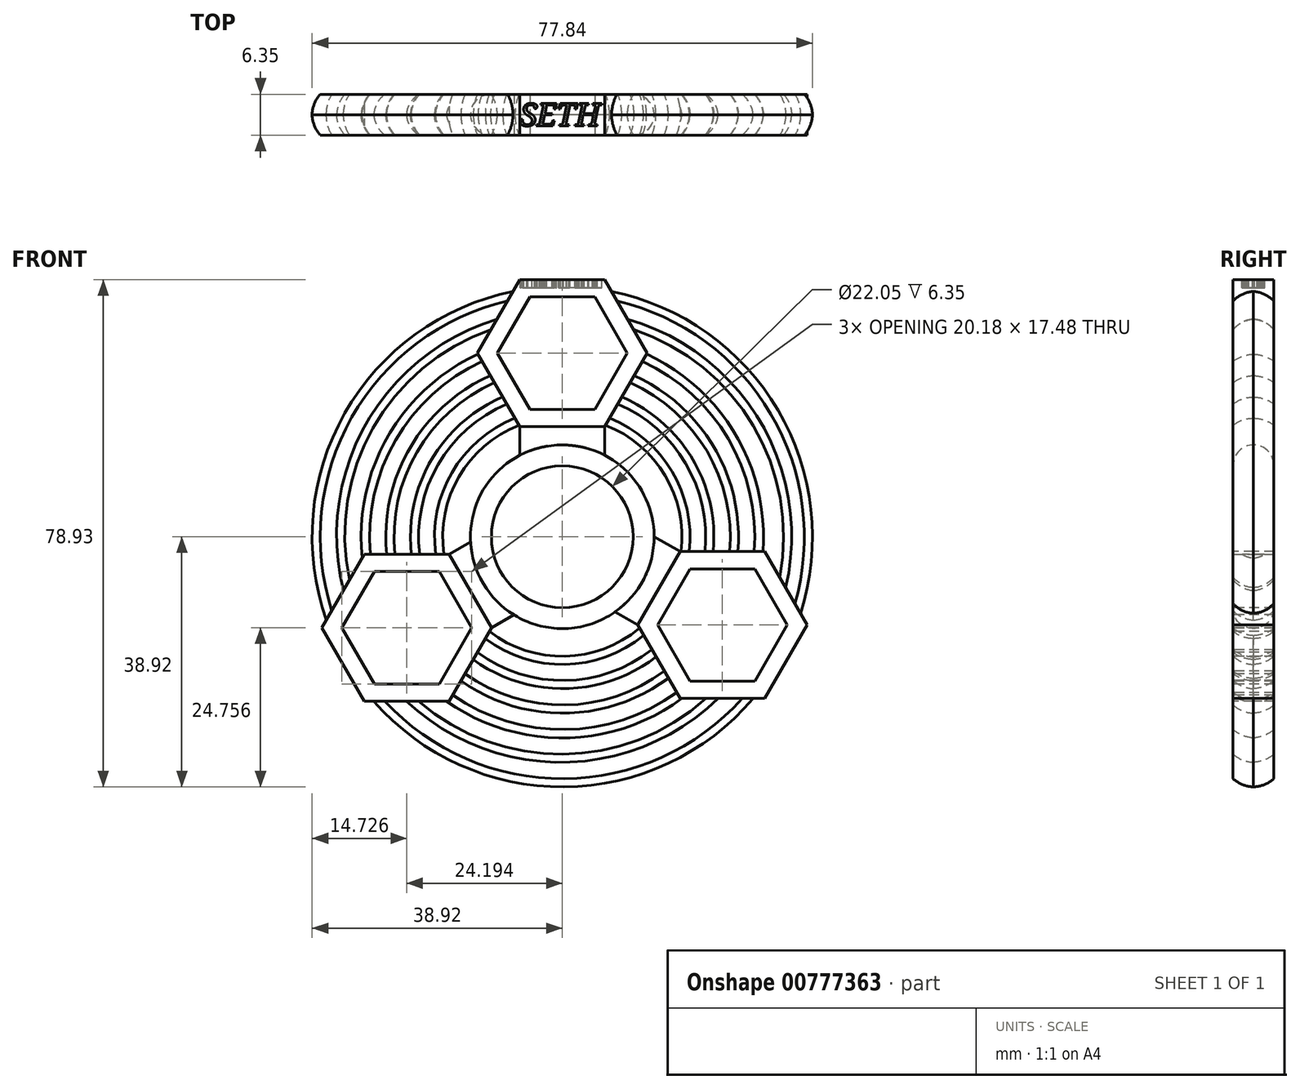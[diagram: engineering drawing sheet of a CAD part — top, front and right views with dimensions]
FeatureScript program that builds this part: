
annotation { "Feature Type Name" : "Feature", "Feature Type Description" : "" }
export const myFeature = defineFeature(function(context is Context, id is Id, definition is map)
    precondition{}
    {
        {
            var Q0;
            Q0=qCreatedBy(makeId("Front.planeOp"),FACE);
            var sketch = newSketch(context, id + "F0", { "sketchPlane" : qUnion([Q0])});
            skCircle(sketch, "E0", {"center": v(0, 0) * mm, "radius": 11.02 * mm});
            skCircle(sketch, "E1", {"center": v(0, 0) * mm, "radius": 14.29 * mm});
            skCircle(sketch, "E2.cCircle", {"center": v(0, 28.58) * mm, "radius": 8.74 * mm, "construction": true});
            skLineSegment(sketch, "E2.0", {"start": v(5.04, 19.84) * mm, "end": v(-5.04, 19.84) * mm});
            skLineSegment(sketch, "E2.1", {"start": v(-5.04, 19.84) * mm, "end": v(-10.09, 28.57) * mm});
            skLineSegment(sketch, "E2.2", {"start": v(-10.09, 28.58) * mm, "end": v(-5.04, 37.31) * mm});
            skLineSegment(sketch, "E2.3", {"start": v(-5.04, 37.31) * mm, "end": v(5.04, 37.31) * mm});
            skLineSegment(sketch, "E2.4", {"start": v(5.04, 37.31) * mm, "end": v(10.09, 28.58) * mm});
            skLineSegment(sketch, "E2.5", {"start": v(10.09, 28.57) * mm, "end": v(5.04, 19.84) * mm});
            skPoint(sketch, "E2.0.midPoint", {"position": v(0, 19.84) * mm});
            skCircle(sketch, "E3.cCircle", {"center": v(0, 28.58) * mm, "radius": 11.43 * mm, "construction": true});
            skLineSegment(sketch, "E3.0", {"start": v(6.6, 17.15) * mm, "end": v(-6.6, 17.14) * mm});
            skLineSegment(sketch, "E3.1", {"start": v(-6.6, 17.15) * mm, "end": v(-13.2, 28.57) * mm});
            skLineSegment(sketch, "E3.2", {"start": v(-13.2, 28.58) * mm, "end": v(-6.6, 40) * mm});
            skLineSegment(sketch, "E3.3", {"start": v(-6.6, 40) * mm, "end": v(6.6, 40) * mm});
            skLineSegment(sketch, "E3.4", {"start": v(6.6, 40) * mm, "end": v(13.2, 28.58) * mm});
            skLineSegment(sketch, "E3.5", {"start": v(13.2, 28.57) * mm, "end": v(6.6, 17.15) * mm});
            skPoint(sketch, "E3.0.midPoint", {"position": v(0, 17.15) * mm});
            skCircle(sketch, "E4.1.0", {"center": v(-24.2, -14.16) * mm, "radius": 8.74 * mm, "construction": true});
            skLineSegment(sketch, "E4.1.1", {"start": v(-19.15, -5.43) * mm, "end": v(-14.1, -14.16) * mm});
            skPoint(sketch, "E4.1.2", {"position": v(-14.3, -8.45) * mm});
            skLineSegment(sketch, "E4.1.3", {"start": v(-19.15, -22.9) * mm, "end": v(-29.24, -22.9) * mm});
            skLineSegment(sketch, "E4.1.4", {"start": v(-30.8, -2.73) * mm, "end": v(-17.6, -2.73) * mm});
            skLineSegment(sketch, "E4.1.5", {"start": v(-37.4, -14.16) * mm, "end": v(-30.8, -2.73) * mm});
            skLineSegment(sketch, "E4.1.6", {"start": v(-30.8, -25.6) * mm, "end": v(-37.4, -14.16) * mm});
            skLineSegment(sketch, "E4.1.7", {"start": v(-14.1, -14.16) * mm, "end": v(-19.15, -22.9) * mm});
            skLineSegment(sketch, "E4.1.8", {"start": v(-29.24, -22.9) * mm, "end": v(-34.28, -14.16) * mm});
            skLineSegment(sketch, "E4.1.9", {"start": v(-34.28, -14.16) * mm, "end": v(-29.24, -5.43) * mm});
            skLineSegment(sketch, "E4.1.10", {"start": v(-29.24, -5.43) * mm, "end": v(-19.15, -5.43) * mm});
            skCircle(sketch, "E4.1.11", {"center": v(-24.2, -14.16) * mm, "radius": 11.43 * mm, "construction": true});
            skLineSegment(sketch, "E4.1.12", {"start": v(-17.6, -2.73) * mm, "end": v(-11, -14.16) * mm});
            skLineSegment(sketch, "E4.1.13", {"start": v(-11, -14.16) * mm, "end": v(-17.6, -25.6) * mm});
            skLineSegment(sketch, "E4.1.14", {"start": v(-17.6, -25.6) * mm, "end": v(-30.8, -25.6) * mm});
            skPoint(sketch, "E4.1.15", {"position": v(-16.63, -9.8) * mm});
            skCircle(sketch, "E4.2.0", {"center": v(24.92, -13.75) * mm, "radius": 8.74 * mm, "construction": true});
            skLineSegment(sketch, "E4.2.1", {"start": v(14.83, -13.75) * mm, "end": v(19.87, -5) * mm});
            skPoint(sketch, "E4.2.2", {"position": v(15.02, -8.03) * mm});
            skLineSegment(sketch, "E4.2.3", {"start": v(29.96, -5) * mm, "end": v(35, -13.75) * mm});
            skLineSegment(sketch, "E4.2.4", {"start": v(18.32, -25.18) * mm, "end": v(11.72, -13.75) * mm});
            skLineSegment(sketch, "E4.2.5", {"start": v(31.51, -25.18) * mm, "end": v(18.32, -25.18) * mm});
            skLineSegment(sketch, "E4.2.6", {"start": v(38.11, -13.75) * mm, "end": v(31.51, -25.18) * mm});
            skLineSegment(sketch, "E4.2.7", {"start": v(19.87, -5) * mm, "end": v(29.96, -5) * mm});
            skLineSegment(sketch, "E4.2.8", {"start": v(35, -13.75) * mm, "end": v(29.96, -22.48) * mm});
            skLineSegment(sketch, "E4.2.9", {"start": v(29.96, -22.48) * mm, "end": v(19.87, -22.48) * mm});
            skLineSegment(sketch, "E4.2.10", {"start": v(19.87, -22.48) * mm, "end": v(14.83, -13.75) * mm});
            skCircle(sketch, "E4.2.11", {"center": v(24.92, -13.75) * mm, "radius": 11.43 * mm, "construction": true});
            skLineSegment(sketch, "E4.2.12", {"start": v(11.72, -13.75) * mm, "end": v(18.32, -2.32) * mm});
            skLineSegment(sketch, "E4.2.13", {"start": v(18.32, -2.32) * mm, "end": v(31.51, -2.32) * mm});
            skLineSegment(sketch, "E4.2.14", {"start": v(31.51, -2.32) * mm, "end": v(38.11, -13.75) * mm});
            skPoint(sketch, "E4.2.15", {"position": v(17.35, -9.38) * mm});
            skPoint(sketch, "E4.center", {"position": v(0.24, 0.22) * mm});
            skSolve(sketch);
        }
        {
            var Q0;
            Q0=qCreatedBy(makeId("Front.planeOp"),FACE);
            var sketch = newSketch(context, id + "F1", { "sketchPlane" : qUnion([Q0])});
            skLineSegment(sketch, "E5.0", {"start": v(-5.04, 19.84) * mm, "end": v(-10.09, 28.57) * mm});
            skLineSegment(sketch, "E5.1", {"start": v(5.04, 19.84) * mm, "end": v(-5.04, 19.84) * mm});
            skLineSegment(sketch, "E5.2", {"start": v(-10.09, 28.58) * mm, "end": v(-5.04, 37.31) * mm});
            skCircle(sketch, "E5.3", {"center": v(0, 28.58) * mm, "radius": 8.74 * mm});
            skLineSegment(sketch, "E5.4", {"start": v(-5.04, 37.31) * mm, "end": v(5.04, 37.31) * mm});
            skLineSegment(sketch, "E5.5", {"start": v(5.04, 37.31) * mm, "end": v(10.09, 28.58) * mm});
            skLineSegment(sketch, "E5.6", {"start": v(18.32, -2.32) * mm, "end": v(31.51, -2.32) * mm});
            skCircle(sketch, "E5.7", {"center": v(-24.2, -14.16) * mm, "radius": 11.43 * mm});
            skCircle(sketch, "E5.8", {"center": v(0, 0) * mm, "radius": 14.29 * mm});
            skCircle(sketch, "E5.9", {"center": v(0, 0) * mm, "radius": 11.02 * mm});
            skLineSegment(sketch, "E5.10", {"start": v(13.2, 28.57) * mm, "end": v(6.6, 17.15) * mm});
            skLineSegment(sketch, "E5.11", {"start": v(6.6, 40) * mm, "end": v(13.2, 28.58) * mm});
            skLineSegment(sketch, "E5.12", {"start": v(-6.6, 40) * mm, "end": v(6.6, 40) * mm});
            skLineSegment(sketch, "E5.13", {"start": v(38.11, -13.75) * mm, "end": v(31.51, -25.18) * mm});
            skLineSegment(sketch, "E5.14", {"start": v(-30.8, -2.73) * mm, "end": v(-17.6, -2.73) * mm});
            skLineSegment(sketch, "E5.15", {"start": v(10.09, 28.57) * mm, "end": v(8.57, 25.94) * mm});
            skCircle(sketch, "E5.16", {"center": v(0, 28.58) * mm, "radius": 11.43 * mm});
            skLineSegment(sketch, "E5.17", {"start": v(6.6, 17.15) * mm, "end": v(-6.6, 17.14) * mm});
            skLineSegment(sketch, "E5.18", {"start": v(-6.6, 17.15) * mm, "end": v(-13.2, 28.57) * mm});
            skLineSegment(sketch, "E5.19", {"start": v(-13.2, 28.58) * mm, "end": v(-6.6, 40) * mm});
            skLineSegment(sketch, "E5.20", {"start": v(31.51, -2.32) * mm, "end": v(38.11, -13.75) * mm});
            skLineSegment(sketch, "E5.21", {"start": v(-17.6, -2.73) * mm, "end": v(-11, -14.16) * mm});
            skLineSegment(sketch, "E5.22", {"start": v(19.87, -22.48) * mm, "end": v(14.83, -13.75) * mm});
            skLineSegment(sketch, "E5.23", {"start": v(-29.24, -22.9) * mm, "end": v(-34.28, -14.16) * mm});
            skLineSegment(sketch, "E5.24", {"start": v(-37.4, -14.16) * mm, "end": v(-30.8, -2.73) * mm});
            skLineSegment(sketch, "E5.25", {"start": v(19.87, -5) * mm, "end": v(29.96, -5) * mm});
            skLineSegment(sketch, "E5.26", {"start": v(-17.6, -25.6) * mm, "end": v(-30.8, -25.6) * mm});
            skCircle(sketch, "E5.27", {"center": v(-24.2, -14.16) * mm, "radius": 8.74 * mm});
            skLineSegment(sketch, "E5.28", {"start": v(29.96, -5) * mm, "end": v(35, -13.75) * mm});
            skLineSegment(sketch, "E5.29", {"start": v(-11, -14.16) * mm, "end": v(-17.6, -25.6) * mm});
            skCircle(sketch, "E5.30", {"center": v(24.92, -13.75) * mm, "radius": 11.43 * mm});
            skLineSegment(sketch, "E5.31", {"start": v(-34.28, -14.16) * mm, "end": v(-29.24, -5.43) * mm});
            skLineSegment(sketch, "E5.32", {"start": v(-30.8, -25.6) * mm, "end": v(-37.4, -14.16) * mm});
            skCircle(sketch, "E5.33", {"center": v(24.92, -13.75) * mm, "radius": 8.74 * mm});
            skLineSegment(sketch, "E5.34", {"start": v(35, -13.75) * mm, "end": v(29.96, -22.48) * mm});
            skLineSegment(sketch, "E5.35", {"start": v(-19.15, -5.43) * mm, "end": v(-14.1, -14.16) * mm});
            skLineSegment(sketch, "E5.36", {"start": v(18.32, -25.18) * mm, "end": v(11.72, -13.75) * mm});
            skLineSegment(sketch, "E5.37", {"start": v(11.72, -13.75) * mm, "end": v(18.32, -2.32) * mm});
            skLineSegment(sketch, "E5.38", {"start": v(-29.24, -5.43) * mm, "end": v(-19.15, -5.43) * mm});
            skLineSegment(sketch, "E5.39", {"start": v(-14.1, -14.16) * mm, "end": v(-19.15, -22.9) * mm});
            skLineSegment(sketch, "E5.40", {"start": v(14.83, -13.75) * mm, "end": v(19.87, -5) * mm});
            skLineSegment(sketch, "E5.41", {"start": v(29.96, -22.48) * mm, "end": v(19.87, -22.48) * mm});
            skLineSegment(sketch, "E5.42", {"start": v(-19.15, -22.9) * mm, "end": v(-29.24, -22.9) * mm});
            skLineSegment(sketch, "E5.43", {"start": v(31.51, -25.18) * mm, "end": v(18.32, -25.18) * mm});
            skArc(sketch, "E6.trimOffspring", {"start": v(-13.85, -19.1) * mm, "mid": v(0.43, -23.64) * mm, "end": v(14.57, -18.7) * mm});
            skArc(sketch, "E7.trimOffspring", {"start": v(-13.2, -18) * mm, "mid": v(0.43, -22.36) * mm, "end": v(13.93, -17.58) * mm});
            skArc(sketch, "E8.trimOffspring", {"start": v(-15.13, -21.32) * mm, "mid": v(0.43, -26.18) * mm, "end": v(15.85, -20.9) * mm});
            skArc(sketch, "E9.trimOffspring", {"start": v(-15.77, -22.43) * mm, "mid": v(0.43, -27.45) * mm, "end": v(16.5, -22.02) * mm});
            skArc(sketch, "E10.trimOffspring", {"start": v(22.19, -2.32) * mm, "mid": v(19.2, 11.4) * mm, "end": v(8.62, 20.65) * mm});
            skArc(sketch, "E11.trimOffspring", {"start": v(23.47, -2.32) * mm, "mid": v(20.3, 12.04) * mm, "end": v(9.26, 21.76) * mm});
            skArc(sketch, "E12.trimOffspring", {"start": v(26.03, -2.32) * mm, "mid": v(22.5, 13.31) * mm, "end": v(10.54, 23.97) * mm});
            skArc(sketch, "E13.trimOffspring", {"start": v(27.31, -2.32) * mm, "mid": v(23.6, 13.95) * mm, "end": v(11.18, 25.08) * mm});
            skArc(sketch, "E14.trimOffspring", {"start": v(-11.18, 25.08) * mm, "mid": v(-23.74, 13.78) * mm, "end": v(-27.31, -2.73) * mm});
            skArc(sketch, "E15.trimOffspring", {"start": v(-10.54, 23.97) * mm, "mid": v(-22.63, 13.14) * mm, "end": v(-26.03, -2.73) * mm});
            skArc(sketch, "E16.trimOffspring", {"start": v(-9.26, 21.76) * mm, "mid": v(-20.43, 11.87) * mm, "end": v(-23.47, -2.73) * mm});
            skArc(sketch, "E17.trimOffspring", {"start": v(-8.62, 20.65) * mm, "mid": v(-19.33, 11.23) * mm, "end": v(-22.19, -2.73) * mm});
            skArc(sketch, "E18.trimOffspring", {"start": v(-22.37, -25.6) * mm, "mid": v(0.08, -33.83) * mm, "end": v(22.37, -25.18) * mm});
            skArc(sketch, "E19.trimOffspring", {"start": v(-24.25, -25.6) * mm, "mid": v(0.08, -35.1) * mm, "end": v(24.25, -25.18) * mm});
            skArc(sketch, "E20.trimOffspring", {"start": v(-17.05, -24.65) * mm, "mid": v(0.43, -30) * mm, "end": v(17.77, -24.23) * mm});
            skArc(sketch, "E21.trimOffspring", {"start": v(34.76, -7.93) * mm, "mid": v(30.82, 17.9) * mm, "end": v(10.15, 33.86) * mm});
            skArc(sketch, "E22.trimOffspring", {"start": v(33.82, -6.3) * mm, "mid": v(29.73, 17.25) * mm, "end": v(11.09, 32.23) * mm});
            skArc(sketch, "E23.trimOffspring", {"start": v(29.87, -2.32) * mm, "mid": v(25.81, 15.22) * mm, "end": v(12.46, 27.3) * mm});
            skArc(sketch, "E24.trimOffspring", {"start": v(-10.15, 33.86) * mm, "mid": v(-30.55, 17.54) * mm, "end": v(-34.03, -8.35) * mm});
            skArc(sketch, "E25.trimOffspring", {"start": v(-11.09, 32.23) * mm, "mid": v(-29.45, 16.9) * mm, "end": v(-33.1, -6.72) * mm});
            skArc(sketch, "E26.trimOffspring", {"start": v(-12.46, 27.3) * mm, "mid": v(-25.94, 15.05) * mm, "end": v(-29.87, -2.73) * mm});
            skLineSegment(sketch, "E27", {"start": v(-6.6, 17.14) * mm, "end": v(-6.6, 12.67) * mm});
            skLineSegment(sketch, "E28", {"start": v(6.6, 17.15) * mm, "end": v(6.6, 12.67) * mm});
            skLineSegment(sketch, "E29", {"start": v(11.72, -13.75) * mm, "end": v(8.19, -11.7) * mm});
            skLineSegment(sketch, "E30", {"start": v(18.32, -2.32) * mm, "end": v(14.29, 0) * mm});
            skLineSegment(sketch, "E31", {"start": v(-17.6, -2.73) * mm, "end": v(-12.84, 0) * mm});
            skLineSegment(sketch, "E32", {"start": v(-11, -14.16) * mm, "end": v(-7.51, -12.15) * mm});
            skLineSegment(sketch, "E33.trimOffspring", {"start": v(7.92, 24.81) * mm, "end": v(5.04, 19.84) * mm});
            skLineSegment(sketch, "E34", {"start": v(7.92, 24.81) * mm, "end": v(8.57, 25.94) * mm});
            skArc(sketch, "E35", {"start": v(-11.98, -15.86) * mm, "mid": v(0.42, -19.87) * mm, "end": v(12.64, -15.34) * mm});
            skArc(sketch, "E36", {"start": v(-11.34, -14.75) * mm, "mid": v(0.42, -18.6) * mm, "end": v(12, -14.22) * mm});
            skArc(sketch, "E37.trimOffspring", {"start": v(-7.36, 18.46) * mm, "mid": v(-17.18, 10) * mm, "end": v(-19.69, -2.73) * mm});
            skArc(sketch, "E38.trimOffspring", {"start": v(-6.72, 17.35) * mm, "mid": v(-16.08, 9.36) * mm, "end": v(-18.4, -2.73) * mm});
            skArc(sketch, "E39.trimOffspring", {"start": v(18.46, -2.32) * mm, "mid": v(15.97, 9.54) * mm, "end": v(6.72, 17.35) * mm});
            skArc(sketch, "E40.trimOffspring", {"start": v(19.74, -2.32) * mm, "mid": v(17.07, 10.17) * mm, "end": v(7.36, 18.46) * mm});
            skArc(sketch, "E41", {"start": v(-8.52, 36.68) * mm, "mid": v(-32.75, 18.58) * mm, "end": v(-35.86, -11.5) * mm});
            skArc(sketch, "E42", {"start": v(-7.66, 38.16) * mm, "mid": v(-33.85, 19.22) * mm, "end": v(-36.7, -12.97) * mm});
            skArc(sketch, "E43.trimOffspring", {"start": v(36.19, -10.41) * mm, "mid": v(32.47, 19.08) * mm, "end": v(8.52, 36.68) * mm});
            skArc(sketch, "E44.trimOffspring", {"start": v(37.06, -11.92) * mm, "mid": v(33.57, 19.7) * mm, "end": v(7.66, 38.16) * mm});
            skArc(sketch, "E45.trimOffspring", {"start": v(-27.62, -25.6) * mm, "mid": v(0.28, -37.65) * mm, "end": v(28, -25.18) * mm});
            skArc(sketch, "E46.trimOffspring", {"start": v(-29.33, -25.6) * mm, "mid": v(0.27, -38.92) * mm, "end": v(29.69, -25.18) * mm});
            skArc(sketch, "E47", {"start": v(-13.11, 28.43) * mm, "mid": v(-27.23, 15.45) * mm, "end": v(-31.13, -3.32) * mm});
            skArc(sketch, "E48.trimOffspring", {"start": v(-18.03, -25.6) * mm, "mid": v(0.36, -31.3) * mm, "end": v(18.6, -25.18) * mm});
            skArc(sketch, "E49.trimOffspring", {"start": v(31.22, -2.32) * mm, "mid": v(26.97, 15.89) * mm, "end": v(13.11, 28.43) * mm});
            skSolve(sketch);
        }
        {
            var Q0;
            Q0 = qSketchRegion(id + "F0", true);
            var Q1;
            {var subQ0=sQuery(id+"F1.wireOp",EDGE,"E41");Q1=makeQuery(id+"F1.imprint","IMPRINT",FACE,{"disambiguationData":[TD([[makeQuery(id+"F1.imprint","IMPRINT",EDGE,{"derivedFrom":subQ0}),-1.0]])]});}
            var Q2;
            {var subQ0=sQuery(id+"F1.wireOp",EDGE,"E24.trimOffspring");Q2=makeQuery(id+"F1.imprint","IMPRINT",FACE,{"disambiguationData":[TD([[makeQuery(id+"F1.imprint","IMPRINT",EDGE,{"derivedFrom":subQ0}),1.0]])]});}
            var Q3;
            {var subQ0=sQuery(id+"F1.wireOp",EDGE,"E14.trimOffspring");Q3=makeQuery(id+"F1.imprint","IMPRINT",FACE,{"disambiguationData":[TD([[makeQuery(id+"F1.imprint","IMPRINT",EDGE,{"derivedFrom":subQ0}),1.0]])]});}
            var Q4;
            {var subQ0=sQuery(id+"F1.wireOp",EDGE,"E16.trimOffspring");Q4=makeQuery(id+"F1.imprint","IMPRINT",FACE,{"disambiguationData":[TD([[makeQuery(id+"F1.imprint","IMPRINT",EDGE,{"derivedFrom":subQ0}),1.0]])]});}
            var Q5;
            {var subQ0=sQuery(id+"F1.wireOp",EDGE,"E37.trimOffspring");Q5=makeQuery(id+"F1.imprint","IMPRINT",FACE,{"disambiguationData":[TD([[makeQuery(id+"F1.imprint","IMPRINT",EDGE,{"derivedFrom":subQ0}),1.0]])]});}
            var Q6;
            {var subQ0=sQuery(id+"F1.wireOp",EDGE,"E39.trimOffspring");Q6=makeQuery(id+"F1.imprint","IMPRINT",FACE,{"disambiguationData":[TD([[makeQuery(id+"F1.imprint","IMPRINT",EDGE,{"derivedFrom":subQ0}),-1.0]])]});}
            var Q7;
            {var subQ0=sQuery(id+"F1.wireOp",EDGE,"E10.trimOffspring");Q7=makeQuery(id+"F1.imprint","IMPRINT",FACE,{"disambiguationData":[TD([[makeQuery(id+"F1.imprint","IMPRINT",EDGE,{"derivedFrom":subQ0}),-1.0]])]});}
            var Q8;
            {var subQ0=sQuery(id+"F1.wireOp",EDGE,"E12.trimOffspring");Q8=makeQuery(id+"F1.imprint","IMPRINT",FACE,{"disambiguationData":[TD([[makeQuery(id+"F1.imprint","IMPRINT",EDGE,{"derivedFrom":subQ0}),-1.0]])]});}
            var Q9;
            {var subQ0=sQuery(id+"F1.wireOp",EDGE,"a1603055-6a45-48f4-a4fc-ce80c4b6e8a6.trimOffspring");Q9=makeQuery(id+"F1.imprint","IMPRINT",FACE,{"disambiguationData":[TD([[makeQuery(id+"F1.imprint","IMPRINT",EDGE,{"derivedFrom":subQ0}),1.0]])]});}
            var Q10;
            {var subQ0=sQuery(id+"F1.wireOp",EDGE,"E21.trimOffspring");Q10=makeQuery(id+"F1.imprint","IMPRINT",FACE,{"disambiguationData":[TD([[makeQuery(id+"F1.imprint","IMPRINT",EDGE,{"derivedFrom":subQ0}),1.0]])]});}
            var Q11;
            {var subQ0=sQuery(id+"F1.wireOp",EDGE,"E43.trimOffspring");Q11=makeQuery(id+"F1.imprint","IMPRINT",FACE,{"disambiguationData":[TD([[makeQuery(id+"F1.imprint","IMPRINT",EDGE,{"derivedFrom":subQ0}),-1.0]])]});}
            var Q12;
            {var subQ6=sQuery(id+"F1.wireOp",EDGE,"E32");Q12=makeQuery(id+"F1.imprint","IMPRINT",FACE,{"disambiguationData":[TD([[makeQuery(id+"F1.imprint","IMPRINT",EDGE,{"derivedFrom":subQ6}),1.0]])]});}
            var Q13;
            {var subQ0=sQuery(id+"F1.wireOp",EDGE,"E27");Q13=makeQuery(id+"F1.imprint","IMPRINT",FACE,{"disambiguationData":[TD([[makeQuery(id+"F1.imprint","IMPRINT",EDGE,{"derivedFrom":subQ0}),1.0]])]});}
            var Q14;
            {var subQ3=sQuery(id+"F1.wireOp",EDGE,"E29");Q14=makeQuery(id+"F1.imprint","IMPRINT",FACE,{"disambiguationData":[TD([[makeQuery(id+"F1.imprint","IMPRINT",EDGE,{"derivedFrom":subQ3}),-1.0]])]});}
            var Q15;
            {var subQ0=sQuery(id+"F1.wireOp",EDGE,"E35");Q15=makeQuery(id+"F1.imprint","IMPRINT",FACE,{"disambiguationData":[TD([[makeQuery(id+"F1.imprint","IMPRINT",EDGE,{"derivedFrom":subQ0}),1.0]])]});}
            var Q16;
            {var subQ0=sQuery(id+"F1.wireOp",EDGE,"E6.trimOffspring");Q16=makeQuery(id+"F1.imprint","IMPRINT",FACE,{"disambiguationData":[TD([[makeQuery(id+"F1.imprint","IMPRINT",EDGE,{"derivedFrom":subQ0}),1.0]])]});}
            var Q17;
            {var subQ0=sQuery(id+"F1.wireOp",EDGE,"E8.trimOffspring");Q17=makeQuery(id+"F1.imprint","IMPRINT",FACE,{"disambiguationData":[TD([[makeQuery(id+"F1.imprint","IMPRINT",EDGE,{"derivedFrom":subQ0}),-1.0]])]});}
            var Q18;
            {var subQ0=sQuery(id+"F1.wireOp",EDGE,"E45.trimOffspring");Q18=makeQuery(id+"F1.imprint","IMPRINT",FACE,{"disambiguationData":[TD([[makeQuery(id+"F1.imprint","IMPRINT",EDGE,{"derivedFrom":subQ0}),-1.0]])]});}
            var Q19;
            {var subQ0=sQuery(id+"F1.wireOp",EDGE,"E18.trimOffspring");Q19=makeQuery(id+"F1.imprint","IMPRINT",FACE,{"disambiguationData":[TD([[makeQuery(id+"F1.imprint","IMPRINT",EDGE,{"derivedFrom":subQ0}),-1.0]])]});}
            var Q20;
            {var subQ0=sQuery(id+"F1.wireOp",EDGE,"E26.trimOffspring");Q20=makeQuery(id+"F1.imprint","IMPRINT",FACE,{"disambiguationData":[TD([[makeQuery(id+"F1.imprint","IMPRINT",EDGE,{"derivedFrom":subQ0}),-1.0]])]});}
            var Q21;
            {var subQ4=sQuery(id+"F1.wireOp",EDGE,"E20.trimOffspring");Q21=makeQuery(id+"F1.imprint","IMPRINT",FACE,{"disambiguationData":[TD([[makeQuery(id+"F1.imprint","IMPRINT",EDGE,{"derivedFrom":subQ4}),-1.0]])]});}
            var Q22;
            {var subQ0=sQuery(id+"F1.wireOp",EDGE,"E23.trimOffspring");Q22=makeQuery(id+"F1.imprint","IMPRINT",FACE,{"disambiguationData":[TD([[makeQuery(id+"F1.imprint","IMPRINT",EDGE,{"derivedFrom":subQ0}),-1.0]])]});}
            extrude(context, id + "F2", {"entities" : qUnion([Q0, Q1, Q2, Q3, Q4, Q5, Q6, Q7, Q8, Q9, Q10, Q11, Q12, Q13, Q14, Q15, Q16, Q17, Q18, Q19, Q20, Q21, Q22]), "oppositeDirection" : true, "depth" : 6.35 * mm, "offsetDistance" : 25.4 * mm});
        }
        {
            var Q0;
            Q0=makeQuery(id+"F2.opExtrude","CAP_EDGE",EDGE,{"disambiguationData":[OSD([sQuery(id+"F1.wireOp",EDGE,"E42")])],"isStart":true});
            var Q1;
            Q1=makeQuery(id+"F2.opExtrude","CAP_EDGE",EDGE,{"disambiguationData":[OSD([sQuery(id+"F1.wireOp",EDGE,"E24.trimOffspring")])],"isStart":true});
            var Q2;
            Q2=makeQuery(id+"F2.opExtrude","CAP_EDGE",EDGE,{"disambiguationData":[OSD([sQuery(id+"F1.wireOp",EDGE,"E47")])],"isStart":true});
            var Q3;
            Q3=makeQuery(id+"F2.opExtrude","CAP_EDGE",EDGE,{"disambiguationData":[OSD([sQuery(id+"F1.wireOp",EDGE,"E14.trimOffspring")])],"isStart":true});
            var Q4;
            Q4=makeQuery(id+"F2.opExtrude","CAP_EDGE",EDGE,{"disambiguationData":[OSD([sQuery(id+"F1.wireOp",EDGE,"E46.trimOffspring")])],"isStart":true});
            var Q5;
            Q5=makeQuery(id+"F2.opExtrude","CAP_EDGE",EDGE,{"disambiguationData":[OSD([sQuery(id+"F1.wireOp",EDGE,"E16.trimOffspring")])],"isStart":true});
            var Q6;
            Q6=makeQuery(id+"F2.opExtrude","CAP_EDGE",EDGE,{"disambiguationData":[OSD([sQuery(id+"F1.wireOp",EDGE,"E37.trimOffspring")])],"isStart":true});
            var Q7;
            Q7=makeQuery(id+"F2.opExtrude","CAP_EDGE",EDGE,{"disambiguationData":[OSD([sQuery(id+"F1.wireOp",EDGE,"E19.trimOffspring")])],"isStart":true});
            var Q8;
            Q8=makeQuery(id+"F2.opExtrude","CAP_EDGE",EDGE,{"disambiguationData":[OSD([sQuery(id+"F1.wireOp",EDGE,"E48.trimOffspring")])],"isStart":true});
            var Q9;
            Q9=makeQuery(id+"F2.opExtrude","CAP_EDGE",EDGE,{"disambiguationData":[OSD([sQuery(id+"F1.wireOp",EDGE,"E9.trimOffspring")])],"isStart":true});
            var Q10;
            Q10=makeQuery(id+"F2.opExtrude","CAP_EDGE",EDGE,{"disambiguationData":[OSD([sQuery(id+"F1.wireOp",EDGE,"E6.trimOffspring")])],"isStart":true});
            var Q11;
            Q11=makeQuery(id+"F2.opExtrude","CAP_EDGE",EDGE,{"disambiguationData":[OSD([sQuery(id+"F1.wireOp",EDGE,"E35")])],"isStart":true});
            var Q12;
            Q12=makeQuery(id+"F2.opExtrude","CAP_EDGE",EDGE,{"disambiguationData":[OSD([sQuery(id+"F1.wireOp",EDGE,"E44.trimOffspring")])],"isStart":true});
            var Q13;
            Q13=makeQuery(id+"F2.opExtrude","CAP_EDGE",EDGE,{"disambiguationData":[OSD([sQuery(id+"F1.wireOp",EDGE,"E21.trimOffspring")])],"isStart":true});
            var Q14;
            Q14=makeQuery(id+"F2.opExtrude","CAP_EDGE",EDGE,{"disambiguationData":[OSD([sQuery(id+"F1.wireOp",EDGE,"E49.trimOffspring")])],"isStart":true});
            var Q15;
            Q15=makeQuery(id+"F2.opExtrude","CAP_EDGE",EDGE,{"disambiguationData":[OSD([sQuery(id+"F1.wireOp",EDGE,"E13.trimOffspring")])],"isStart":true});
            var Q16;
            Q16=makeQuery(id+"F2.opExtrude","CAP_EDGE",EDGE,{"disambiguationData":[OSD([sQuery(id+"F1.wireOp",EDGE,"E11.trimOffspring")])],"isStart":true});
            var Q17;
            Q17=makeQuery(id+"F2.opExtrude","CAP_EDGE",EDGE,{"disambiguationData":[OSD([sQuery(id+"F1.wireOp",EDGE,"E40.trimOffspring")])],"isStart":true});
            var Q18;
            Q18=makeQuery(id+"F2.opExtrude","CAP_EDGE",EDGE,{"disambiguationData":[OSD([sQuery(id+"F1.wireOp",EDGE,"E44.trimOffspring")])],"isStart":false});
            var Q19;
            Q19=makeQuery(id+"F2.opExtrude","CAP_EDGE",EDGE,{"disambiguationData":[OSD([sQuery(id+"F1.wireOp",EDGE,"E49.trimOffspring")])],"isStart":false});
            var Q20;
            Q20=makeQuery(id+"F2.opExtrude","CAP_EDGE",EDGE,{"disambiguationData":[OSD([sQuery(id+"F1.wireOp",EDGE,"E13.trimOffspring")])],"isStart":false});
            var Q21;
            Q21=makeQuery(id+"F2.opExtrude","CAP_EDGE",EDGE,{"disambiguationData":[OSD([sQuery(id+"F1.wireOp",EDGE,"E11.trimOffspring")])],"isStart":false});
            var Q22;
            Q22=makeQuery(id+"F2.opExtrude","CAP_EDGE",EDGE,{"disambiguationData":[OSD([sQuery(id+"F1.wireOp",EDGE,"E40.trimOffspring")])],"isStart":false});
            var Q23;
            Q23=makeQuery(id+"F2.opExtrude","CAP_EDGE",EDGE,{"disambiguationData":[OSD([sQuery(id+"F1.wireOp",EDGE,"E37.trimOffspring")])],"isStart":false});
            var Q24;
            Q24=makeQuery(id+"F2.opExtrude","CAP_EDGE",EDGE,{"disambiguationData":[OSD([sQuery(id+"F1.wireOp",EDGE,"E16.trimOffspring")])],"isStart":false});
            var Q25;
            Q25=makeQuery(id+"F2.opExtrude","CAP_EDGE",EDGE,{"disambiguationData":[OSD([sQuery(id+"F1.wireOp",EDGE,"E14.trimOffspring")])],"isStart":false});
            var Q26;
            Q26=makeQuery(id+"F2.opExtrude","CAP_EDGE",EDGE,{"disambiguationData":[OSD([sQuery(id+"F1.wireOp",EDGE,"E47")])],"isStart":false});
            var Q27;
            Q27=makeQuery(id+"F2.opExtrude","CAP_EDGE",EDGE,{"disambiguationData":[OSD([sQuery(id+"F1.wireOp",EDGE,"E24.trimOffspring")])],"isStart":false});
            var Q28;
            Q28=makeQuery(id+"F2.opExtrude","CAP_EDGE",EDGE,{"disambiguationData":[OSD([sQuery(id+"F1.wireOp",EDGE,"E42")])],"isStart":false});
            var Q29;
            Q29=makeQuery(id+"F2.opExtrude","CAP_EDGE",EDGE,{"disambiguationData":[OSD([sQuery(id+"F1.wireOp",EDGE,"E46.trimOffspring")])],"isStart":false});
            var Q30;
            Q30=makeQuery(id+"F2.opExtrude","CAP_EDGE",EDGE,{"disambiguationData":[OSD([sQuery(id+"F1.wireOp",EDGE,"E19.trimOffspring")])],"isStart":false});
            var Q31;
            Q31=makeQuery(id+"F2.opExtrude","CAP_EDGE",EDGE,{"disambiguationData":[OSD([sQuery(id+"F1.wireOp",EDGE,"E48.trimOffspring")])],"isStart":false});
            var Q32;
            Q32=makeQuery(id+"F2.opExtrude","CAP_EDGE",EDGE,{"disambiguationData":[OSD([sQuery(id+"F1.wireOp",EDGE,"E9.trimOffspring")])],"isStart":false});
            var Q33;
            Q33=makeQuery(id+"F2.opExtrude","CAP_EDGE",EDGE,{"disambiguationData":[OSD([sQuery(id+"F1.wireOp",EDGE,"E6.trimOffspring")])],"isStart":false});
            var Q34;
            Q34=makeQuery(id+"F2.opExtrude","CAP_EDGE",EDGE,{"disambiguationData":[OSD([sQuery(id+"F1.wireOp",EDGE,"E35")])],"isStart":false});
            var Q35;
            Q35=makeQuery(id+"F2.opExtrude","CAP_EDGE",EDGE,{"disambiguationData":[OSD([sQuery(id+"F1.wireOp",EDGE,"E21.trimOffspring")])],"isStart":false});
            fillet(context, id + "F3", {"entities" : qUnion([Q0, Q1, Q2, Q3, Q4, Q5, Q6, Q7, Q8, Q9, Q10, Q11, Q12, Q13, Q14, Q15, Q16, Q17, Q18, Q19, Q20, Q21, Q22, Q23, Q24, Q25, Q26, Q27, Q28, Q29, Q30, Q31, Q32, Q33, Q34, Q35]), "radius" : 5.08 * mm, "tangentPropagation" : true, "allowEdgeOverflow" : false});
        }
        {
            var Q0;
            Q0=makeQuery(id+"F2.opExtrude","CAP_EDGE",EDGE,{"disambiguationData":[OSD([sQuery(id+"F0.wireOp",EDGE,"E1")])],"isStart":true});
            var Q1;
            Q1=makeQuery(id+"F2.opExtrude","CAP_EDGE",EDGE,{"disambiguationData":[OSD([sQuery(id+"F0.wireOp",EDGE,"E1")])],"isStart":false});
            fillet(context, id + "F4", {"entities" : qUnion([Q0, Q1]), "radius" : 3.17 * mm, "tangentPropagation" : true, "allowEdgeOverflow" : false});
        }
        {
            var Q0;
            Q0=makeQuery(id+"F2.opExtrude","SWEPT_FACE",FACE,{"disambiguationData":[OSD([sQuery(id+"F0.wireOp",EDGE,"E3.3")])]});
            var sketch = newSketch(context, id + "F5", { "sketchPlane" : qUnion([Q0])});
            skText(sketch, "E50", { "text": "SETH", "fontName": "NotoSerif-Italic.ttf"});
            const initialGuessF5  = {"E50": [-0.0066, 0.00143, 1, 0, 0.0035]};
            skSetInitialGuess(sketch, initialGuessF5);
            skSolve(sketch);
        }
        {
            var Q0;
            Q0=makeQuery(id+"F5.imprint","IMPRINT",FACE,{"disambiguationData":[TD([[makeQuery(id+"F5.imprint","IMPRINT",EDGE,{"derivedFrom":sQuery(id+"F5.wireOp",EDGE,"E50.sketch_text.stroke-0")}),-1.0]])]});
            var Q1;
            Q1=makeQuery(id+"F5.imprint","IMPRINT",FACE,{"disambiguationData":[TD([[makeQuery(id+"F5.imprint","IMPRINT",EDGE,{"derivedFrom":sQuery(id+"F5.wireOp",EDGE,"E50.sketch_text.stroke-27")}),-1.0]])]});
            var Q2;
            Q2=makeQuery(id+"F5.imprint","IMPRINT",FACE,{"disambiguationData":[TD([[makeQuery(id+"F5.imprint","IMPRINT",EDGE,{"derivedFrom":sQuery(id+"F5.wireOp",EDGE,"E50.sketch_text.stroke-55")}),-1.0]])]});
            var Q3;
            Q3=makeQuery(id+"F5.imprint","IMPRINT",FACE,{"disambiguationData":[TD([[makeQuery(id+"F5.imprint","IMPRINT",EDGE,{"derivedFrom":sQuery(id+"F5.wireOp",EDGE,"E50.sketch_text.stroke-77")}),-1.0]])]});
            extrude(context, id + "F6", {"entities" : qUnion([Q0, Q1, Q2, Q3]), "operationType" : NewBodyOperationType.REMOVE, "oppositeDirection" : true, "depth" : 1.27 * mm, "offsetDistance" : 25.4 * mm});
        }
    });
